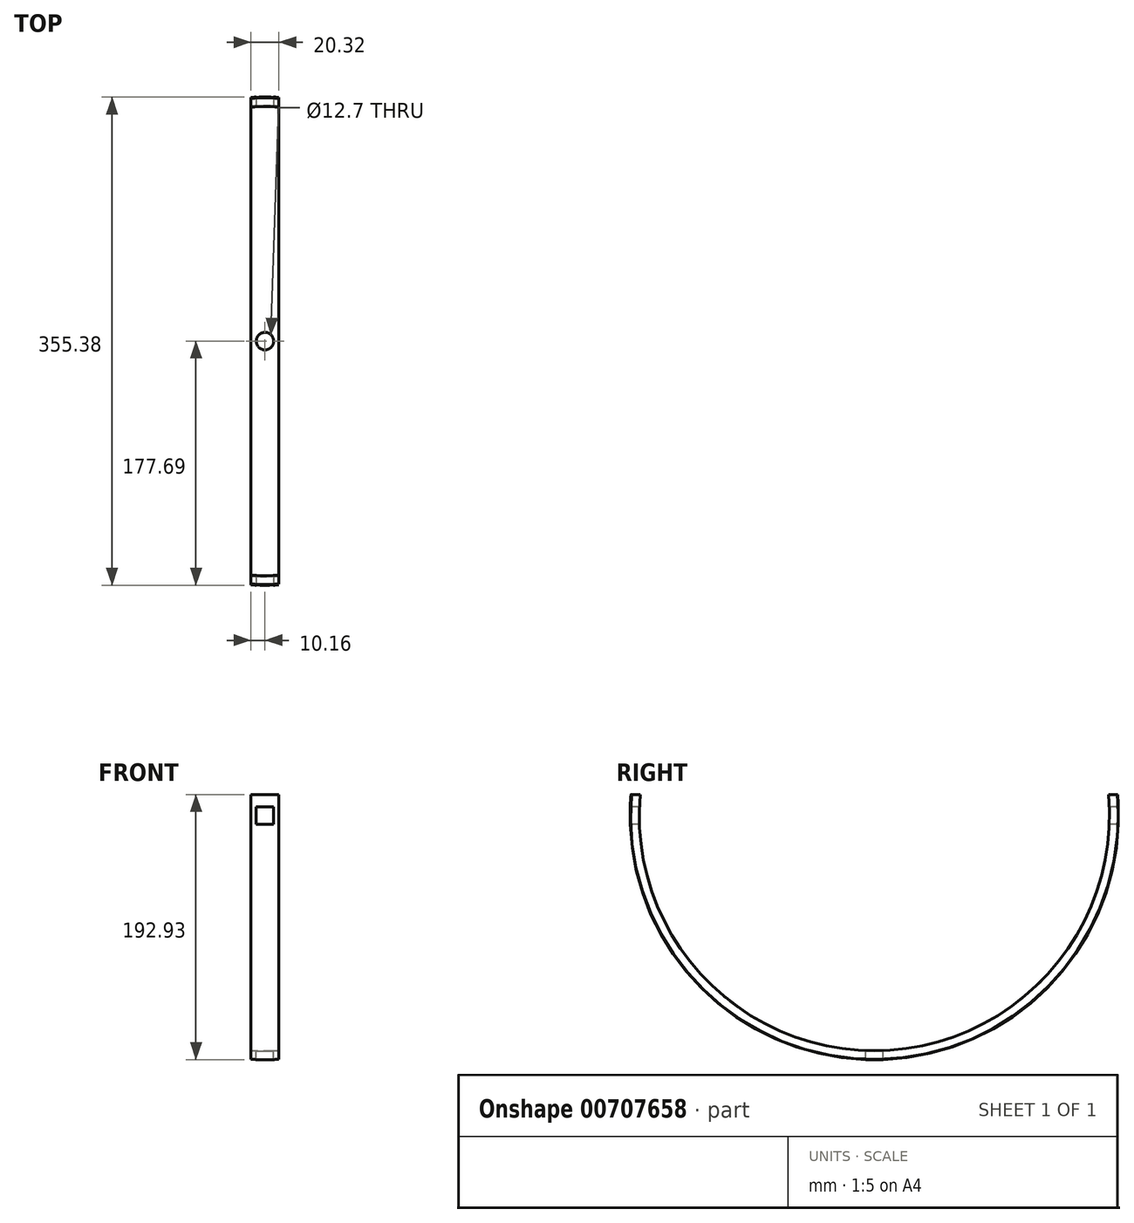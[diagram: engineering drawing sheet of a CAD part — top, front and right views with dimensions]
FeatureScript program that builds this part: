
annotation { "Feature Type Name" : "Feature", "Feature Type Description" : "" }
export const myFeature = defineFeature(function(context is Context, id is Id, definition is map)
    precondition{}
    {
        {
            var Q0;
            Q0=qCreatedBy(makeId("Right.planeOp"),FACE);
            var sketch = newSketch(context, id + "F0", { "sketchPlane" : qUnion([Q0])});
            skArc(sketch, "E0", {"start": v(0, -177.8) * mm, "mid": v(131, -120.21) * mm, "end": v(177.15, 15.24) * mm});
            skArc(sketch, "E1", {"start": v(0, -171.45) * mm, "mid": v(126.5, -115.72) * mm, "end": v(170.77, 15.24) * mm});
            skLineSegment(sketch, "E2", {"start": v(0, 0) * mm, "end": v(81.94, 0) * mm, "construction": true});
            skPoint(sketch, "E3.orphan", {"position": v(0, 75.26) * mm});
            skLineSegment(sketch, "E4.trimOffspring", {"start": v(170.77, 15.24) * mm, "end": v(177.15, 15.24) * mm});
            skPoint(sketch, "E5.orphan", {"position": v(-68.17, 0) * mm});
            skLineSegment(sketch, "E6.trimOffspring", {"start": v(0, -171.45) * mm, "end": v(0, -177.8) * mm});
            skLineSegment(sketch, "E7", {"start": v(0, 0) * mm, "end": v(0, 55.65) * mm, "construction": true});
            skSolve(sketch);
        }
        {
            var Q0;
            Q0=makeQuery(id+"F0.imprint","IMPRINT",FACE,{"disambiguationData":[TD([[makeQuery(id+"F0.imprint","IMPRINT",EDGE,{"derivedFrom":sQuery(id+"F0.wireOp",EDGE,"E0")}),1.0]])]});
            var Q1;
            Q1=sQuery(id+"F0.wireOp",EDGE,"E7");
            revolve(context, id + "F1", {"surfaceOperationType" : NewSurfaceOperationType.NEW, "entities" : qUnion([Q0]), "axis" : qUnion([Q1]), "revolveType" : RevolveType.FULL, "oppositeDirection" : true});
        }
        {
            var Q0;
            Q0=qCreatedBy(makeId("Top.planeOp"),FACE);
            var sketch = newSketch(context, id + "F2", { "sketchPlane" : qUnion([Q0])});
            skCircle(sketch, "E8", {"center": v(0, 0) * mm, "radius": 254 * mm});
            skLineSegment(sketch, "E9", {"start": v(0, 88.49) * mm, "end": v(0, -119.53) * mm, "construction": true});
            skLineSegment(sketch, "E10", {"start": v(-103.33, 0) * mm, "end": v(128.58, 0) * mm, "construction": true});
            skLineSegment(sketch, "E11", {"start": v(10.16, 253.8) * mm, "end": v(10.16, 10.16) * mm});
            skLineSegment(sketch, "E12", {"start": v(10.16, -10.16) * mm, "end": v(10.16, -253.8) * mm});
            skLineSegment(sketch, "E13", {"start": v(-10.16, 253.8) * mm, "end": v(-10.16, -253.8) * mm});
            skLineSegment(sketch, "E14", {"start": v(10.16, -10.16) * mm, "end": v(10.16, 10.16) * mm});
            skSolve(sketch);
        }
        {
            var Q0;
            {var subQ0=sQuery(id+"F2.wireOp",EDGE,"E11");Q0=makeQuery(id+"F2.imprint","IMPRINT",FACE,{"disambiguationData":[TD([[makeQuery(id+"F2.imprint","IMPRINT",EDGE,{"derivedFrom":subQ0}),1.0]])]});}
            var Q1;
            {var subQ0=sQuery(id+"F2.wireOp",EDGE,"M2RqoN3g-rlq5-Dqvl-Py1z-pSIghlXKqAgU");Q1=makeQuery(id+"F2.imprint","IMPRINT",FACE,{"disambiguationData":[TD([[makeQuery(id+"F2.imprint","IMPRINT",EDGE,{"derivedFrom":subQ0}),1.0]])]});}
            var Q2;
            {var subQ0=sQuery(id+"F2.wireOp",EDGE,"E13");Q2=makeQuery(id+"F2.imprint","IMPRINT",FACE,{"disambiguationData":[TD([[makeQuery(id+"F2.imprint","IMPRINT",EDGE,{"derivedFrom":subQ0}),-1.0]])]});}
            extrude(context, id + "F3", {"entities" : qUnion([Q0, Q1, Q2]), "operationType" : NewBodyOperationType.REMOVE, "endBound" : BoundingType.SYMMETRIC, "oppositeDirection" : true, "depth" : 762 * mm, "offsetDistance" : 25.4 * mm});
        }
        {
            var Q0;
            Q0=qCreatedBy(makeId("Front.planeOp"),FACE);
            var sketch = newSketch(context, id + "F4", { "sketchPlane" : qUnion([Q0])});
            skLineSegment(sketch, "E15.bottom", {"start": v(-6.35, -6.35) * mm, "end": v(6.35, -6.35) * mm});
            skLineSegment(sketch, "E15.top", {"start": v(-6.35, 6.35) * mm, "end": v(6.35, 6.35) * mm});
            skLineSegment(sketch, "E15.left", {"start": v(-6.35, -6.35) * mm, "end": v(-6.35, 6.35) * mm});
            skLineSegment(sketch, "E15.right", {"start": v(6.35, -6.35) * mm, "end": v(6.35, 6.35) * mm});
            skSolve(sketch);
        }
        {
            var Q0;
            Q0 = qSketchRegion(id + "F4", true);
            extrude(context, id + "F5", {"entities" : qUnion([Q0]), "operationType" : NewBodyOperationType.REMOVE, "endBound" : BoundingType.SYMMETRIC, "oppositeDirection" : true, "depth" : 762 * mm, "offsetDistance" : 25.4 * mm});
        }
        {
            var Q0;
            Q0=qCreatedBy(makeId("Top.planeOp"),FACE);
            var sketch = newSketch(context, id + "F6", { "sketchPlane" : qUnion([Q0])});
            skCircle(sketch, "E16", {"center": v(0, 0) * mm, "radius": 6.35 * mm});
            skSolve(sketch);
        }
        {
            var Q0;
            Q0 = qSketchRegion(id + "F6", true);
            extrude(context, id + "F7", {"entities" : qUnion([Q0]), "operationType" : NewBodyOperationType.REMOVE, "oppositeDirection" : true, "depth" : 209.3 * mm, "offsetDistance" : 25.4 * mm});
        }
    });
